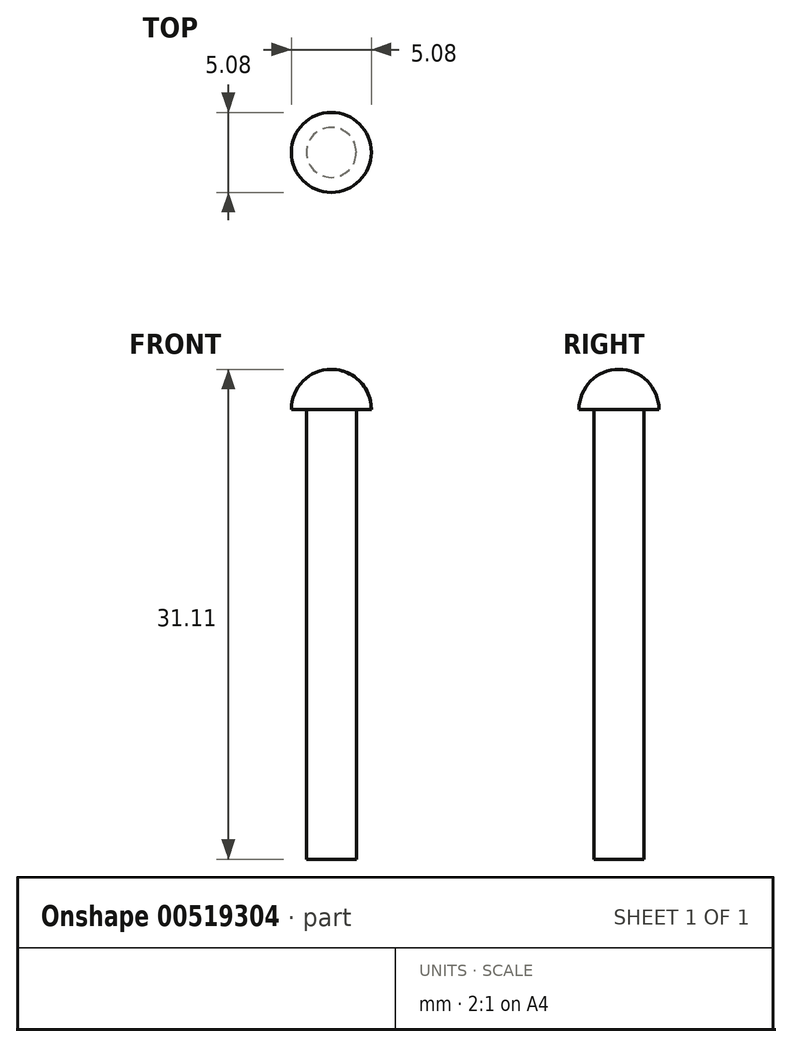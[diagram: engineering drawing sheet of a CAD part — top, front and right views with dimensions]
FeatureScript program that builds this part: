
annotation { "Feature Type Name" : "Feature", "Feature Type Description" : "" }
export const myFeature = defineFeature(function(context is Context, id is Id, definition is map)
    precondition{}
    {
        {
            var Q0;
            Q0=qCreatedBy(makeId("Front.planeOp"),FACE);
            var sketch = newSketch(context, id + "F0", { "sketchPlane" : qUnion([Q0])});
            skLineSegment(sketch, "E0.bottom", {"start": v(0, 0) * mm, "end": v(1.59, 0) * mm});
            skLineSegment(sketch, "E0.left", {"start": v(0, 0) * mm, "end": v(0, 28.58) * mm});
            skLineSegment(sketch, "E0.right", {"start": v(1.59, 0) * mm, "end": v(1.59, 28.58) * mm});
            skArc(sketch, "E1", {"start": v(2.54, 28.58) * mm, "mid": v(1.8, 30.37) * mm, "end": v(0, 31.12) * mm});
            skLineSegment(sketch, "E2", {"start": v(1.59, 28.58) * mm, "end": v(2.54, 28.58) * mm});
            skLineSegment(sketch, "E3", {"start": v(0, 31.12) * mm, "end": v(0, 28.58) * mm});
            skSolve(sketch);
        }
        {
            var Q0;
            Q0 = qSketchRegion(id + "F0", true);
            var Q1;
            Q1=sQuery(id+"F0.wireOp",EDGE,"E0.left");
            revolve(context, id + "F1", {"entities" : qUnion([Q0]), "axis" : qUnion([Q1]), "revolveType" : RevolveType.FULL});
        }
    });
